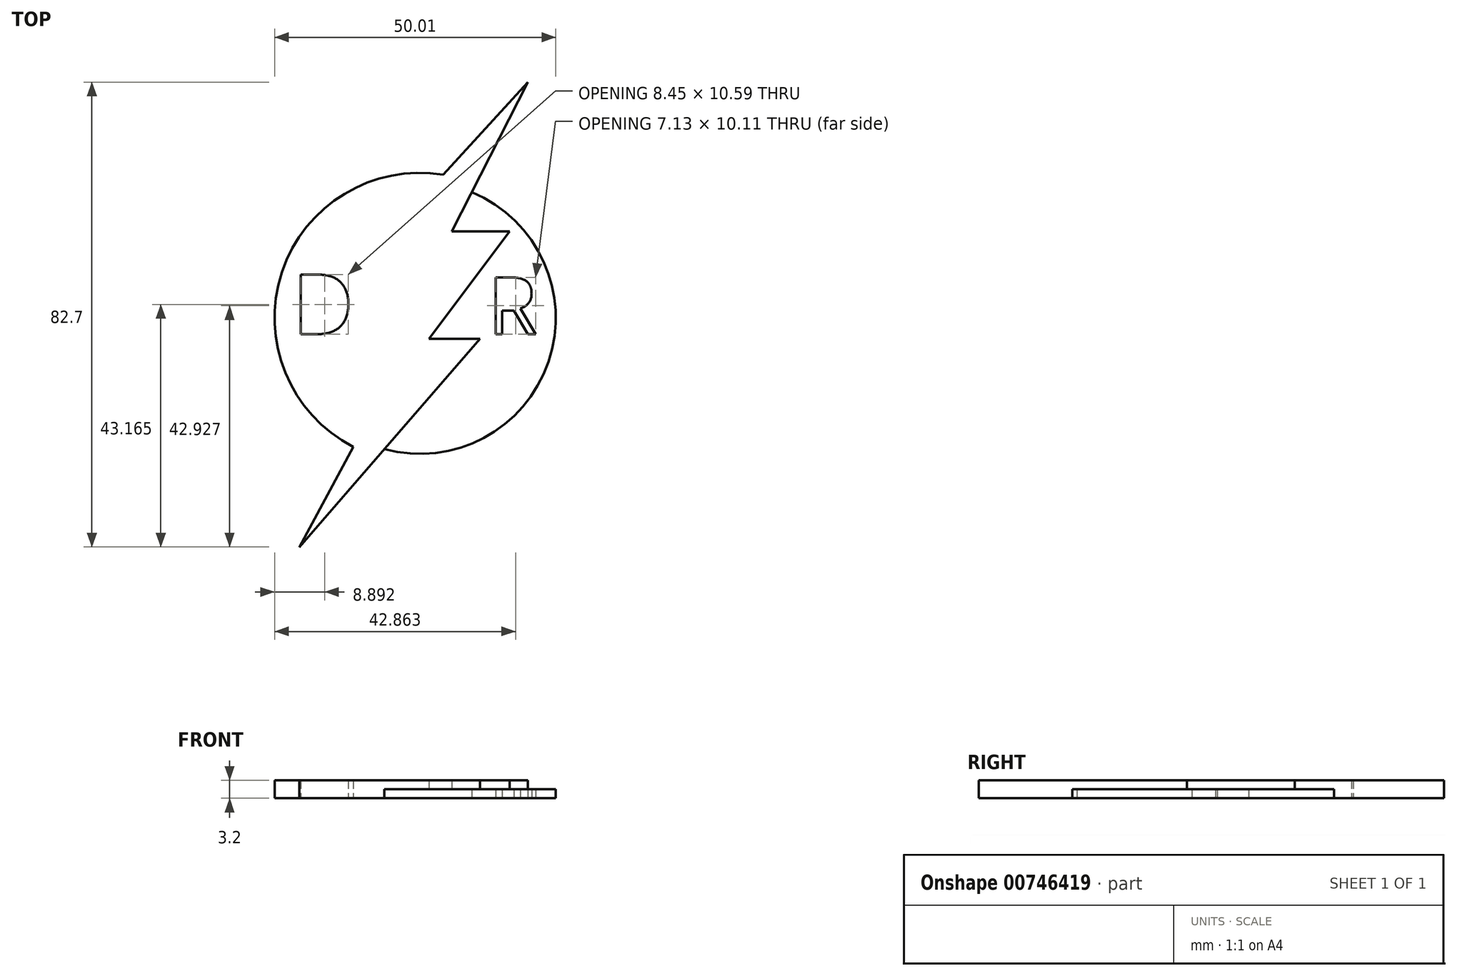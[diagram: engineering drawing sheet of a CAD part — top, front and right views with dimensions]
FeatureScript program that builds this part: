
annotation { "Feature Type Name" : "Feature", "Feature Type Description" : "" }
export const myFeature = defineFeature(function(context is Context, id is Id, definition is map)
    precondition{}
    {
        {
            var Q0;
            Q0=qCreatedBy(makeId("Top.planeOp"),FACE);
            var sketch = newSketch(context, id + "F0", { "sketchPlane" : qUnion([Q0])});
            skArc(sketch, "E0", {"start": v(2.87, 24.03) * mm, "mid": v(-23.14, 7.06) * mm, "end": v(-11.03, -21.54) * mm});
            skLineSegment(sketch, "E1", {"start": v(19.2, 41.92) * mm, "end": v(-12.03, 7.7) * mm});
            skLineSegment(sketch, "E2", {"start": v(-12.03, 7.7) * mm, "end": v(-2.07, 7.7) * mm});
            skLineSegment(sketch, "E3", {"start": v(-2.07, 7.7) * mm, "end": v(-18.23, -9.2) * mm});
            skLineSegment(sketch, "E4", {"start": v(-18.23, -9.2) * mm, "end": v(-4.37, -9.2) * mm});
            skLineSegment(sketch, "E5", {"start": v(-4.37, -9.2) * mm, "end": v(-21.43, -40.78) * mm});
            skLineSegment(sketch, "E6", {"start": v(-21.43, -40.78) * mm, "end": v(10.7, -3.76) * mm});
            skLineSegment(sketch, "E7", {"start": v(10.7, -3.76) * mm, "end": v(1.67, -3.76) * mm});
            skLineSegment(sketch, "E8", {"start": v(1.67, -3.76) * mm, "end": v(15.98, 15.41) * mm});
            skLineSegment(sketch, "E9", {"start": v(15.98, 15.41) * mm, "end": v(5.73, 15.41) * mm});
            skLineSegment(sketch, "E10", {"start": v(5.73, 15.41) * mm, "end": v(19.2, 41.92) * mm});
            skArc(sketch, "E11", {"start": v(4.19, 25.46) * mm, "mid": v(-24.5, 8.09) * mm, "end": v(-11.8, -22.95) * mm});
            skText(sketch, "E12", { "text": "D", "fontName": "OpenSans-Regular.ttf"});
            skText(sketch, "E13", { "text": "R\n", "fontName": "OpenSans-Regular.ttf"});
            skArc(sketch, "E14.trimOffspring", {"start": v(-7.47, -24.7) * mm, "mid": v(24.28, -8.74) * mm, "end": v(10, 23.8) * mm});
            skArc(sketch, "E15.trimOffspring", {"start": v(-6.3, -23.36) * mm, "mid": v(22.9, -7.8) * mm, "end": v(9.26, 22.36) * mm});
            const initialGuessF0  = {"E12": [-0.0226, -0.00291, 1, 0, 0.01068], "E13": [0.0121, -0.00291, 1, 0, 0.0102]};
            skSetInitialGuess(sketch, initialGuessF0);
            skSolve(sketch);
        }
        {
            var Q0;
            Q0=makeQuery(id+"F0.imprint","IMPRINT",FACE,{"disambiguationData":[TD([[makeQuery(id+"F0.imprint","IMPRINT",EDGE,{"derivedFrom":sQuery(id+"F0.wireOp",EDGE,"E0")}),1.0]])]});
            var Q1;
            {var subQ0=sQuery(id+"F0.wireOp",EDGE,"E5");var subQ1=sQuery(id+"F0.wireOp",EDGE,"E0");var subQ2=makeQuery(id+"F0.imprint","INTERSECT",VERTEX,{"derivedFrom":[subQ1,subQ0]});Q1=makeQuery(id+"F0.imprint","IMPRINT",FACE,{"disambiguationData":[TD([[makeQuery(id+"F0.imprint","IMPRINT",EDGE,{"disambiguationData":[TD([[subQ2,-1.0]])],"derivedFrom":subQ1}),-1.0]])]});}
            var Q2;
            {var subQ0=sQuery(id+"F0.wireOp",EDGE,"E1");var subQ1=sQuery(id+"F0.wireOp",EDGE,"E0");var subQ2=makeQuery(id+"F0.imprint","INTERSECT",VERTEX,{"derivedFrom":[subQ1,subQ0]});Q2=makeQuery(id+"F0.imprint","IMPRINT",FACE,{"disambiguationData":[TD([[makeQuery(id+"F0.imprint","IMPRINT",EDGE,{"disambiguationData":[TD([[subQ2,1.0]])],"derivedFrom":subQ1}),-1.0]])]});}
            var Q3;
            {var subQ0=sQuery(id+"F0.wireOp",EDGE,"E10");var subQ1=sQuery(id+"F0.wireOp",EDGE,"E1");var subQ2=makeQuery(id+"F0.imprint","INTERSECT",VERTEX,{"derivedFrom":[subQ1,subQ0]});Q3=makeQuery(id+"F0.imprint","IMPRINT",FACE,{"disambiguationData":[TD([[makeQuery(id+"F0.imprint","IMPRINT",EDGE,{"disambiguationData":[TD([[subQ2,-1.0]])],"derivedFrom":subQ1}),1.0]])]});}
            var Q4;
            {var subQ0=sQuery(id+"F0.wireOp",EDGE,"E6");var subQ1=sQuery(id+"F0.wireOp",EDGE,"E5");var subQ2=makeQuery(id+"F0.imprint","INTERSECT",VERTEX,{"derivedFrom":[subQ1,subQ0]});Q4=makeQuery(id+"F0.imprint","IMPRINT",FACE,{"disambiguationData":[TD([[makeQuery(id+"F0.imprint","IMPRINT",EDGE,{"disambiguationData":[TD([[subQ2,1.0]])],"derivedFrom":subQ1}),1.0]])]});}
            extrude(context, id + "F1", {"entities" : qUnion([Q0, Q1, Q2, Q3, Q4]), "depth" : 3.2 * mm});
        }
        {
            var Q0;
            {var subQ5=sQuery(id+"F0.wireOp",EDGE,"E7");Q0=makeQuery(id+"F0.imprint","IMPRINT",FACE,{"disambiguationData":[TD([[makeQuery(id+"F0.imprint","IMPRINT",EDGE,{"derivedFrom":subQ5}),-1.0]])]});}
            var Q1;
            {var subQ0=sQuery(id+"F0.wireOp",EDGE,"E2");Q1=makeQuery(id+"F0.imprint","IMPRINT",FACE,{"disambiguationData":[TD([[makeQuery(id+"F0.imprint","IMPRINT",EDGE,{"derivedFrom":subQ0}),-1.0]])]});}
            extrude(context, id + "F2", {"entities" : qUnion([Q0, Q1]), "operationType" : NewBodyOperationType.ADD, "depth" : 1.6 * mm});
        }
        {
            var Q0;
            {var subQ0=sQuery(id+"F0.wireOp",EDGE,"E1");var subQ1=sQuery(id+"F0.wireOp",EDGE,"E0");var subQ2=makeQuery(id+"F0.imprint","INTERSECT",VERTEX,{"derivedFrom":[subQ1,subQ0]});Q0=makeQuery(id+"F0.imprint","IMPRINT",FACE,{"disambiguationData":[TD([[makeQuery(id+"F0.imprint","IMPRINT",EDGE,{"disambiguationData":[TD([[subQ2,-1.0]])],"derivedFrom":subQ1}),-1.0]])]});}
            var Q1;
            {var subQ0=sQuery(id+"F0.wireOp",EDGE,"E10");var subQ1=sQuery(id+"F0.wireOp",EDGE,"E0");var subQ2=makeQuery(id+"F0.imprint","INTERSECT",VERTEX,{"derivedFrom":[subQ1,subQ0]});Q1=makeQuery(id+"F0.imprint","IMPRINT",FACE,{"disambiguationData":[TD([[makeQuery(id+"F0.imprint","IMPRINT",EDGE,{"disambiguationData":[TD([[subQ2,1.0]])],"derivedFrom":subQ1}),-1.0]])]});}
            extrude(context, id + "F3", {"entities" : qUnion([Q0, Q1]), "operationType" : NewBodyOperationType.ADD, "depth" : 2.5 * mm});
        }
    });
